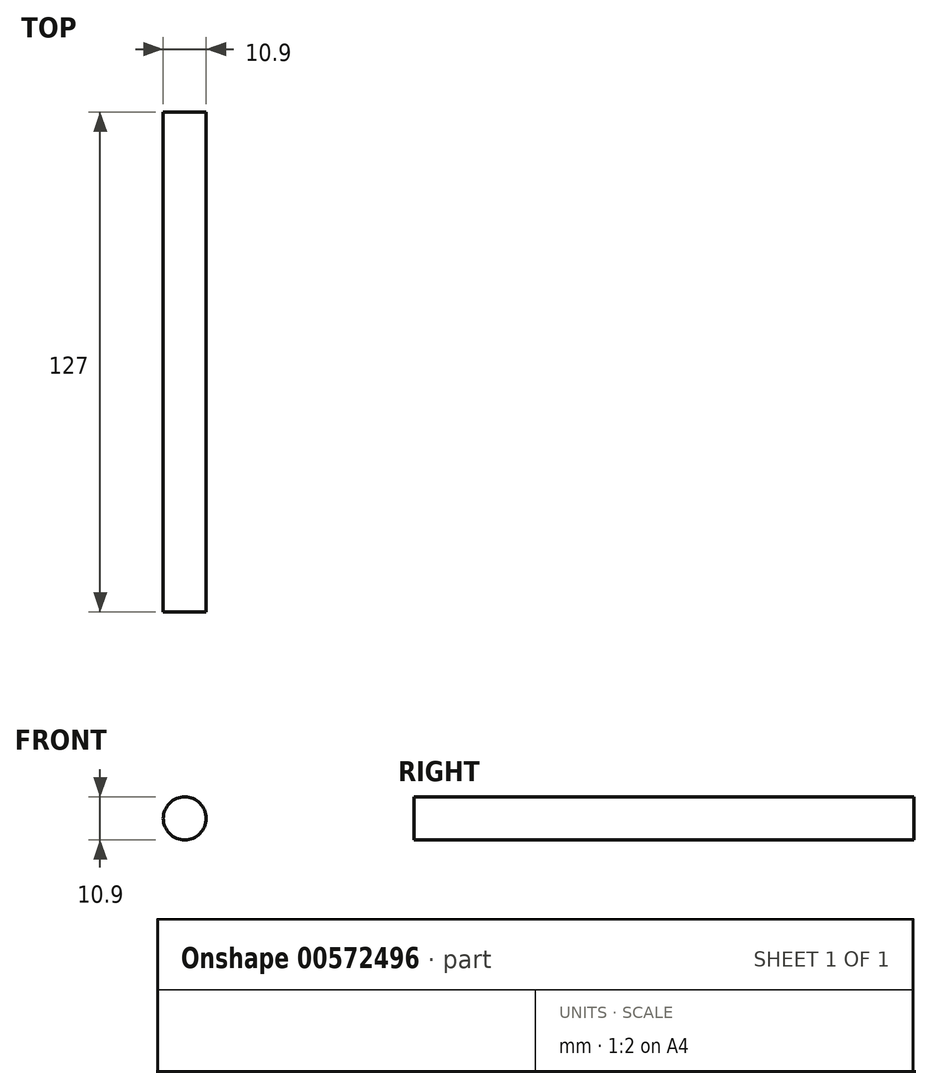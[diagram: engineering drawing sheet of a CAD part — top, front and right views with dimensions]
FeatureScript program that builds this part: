
annotation { "Feature Type Name" : "Feature", "Feature Type Description" : "" }
export const myFeature = defineFeature(function(context is Context, id is Id, definition is map)
    precondition{}
    {
        {
            var Q0;
            Q0=qCreatedBy(makeId("Front.planeOp"),FACE);
            var sketch = newSketch(context, id + "F0", { "sketchPlane" : qUnion([Q0])});
            skCircle(sketch, "E0", {"center": v(-4.03, 13.53) * mm, "radius": 5.45 * mm});
            skSolve(sketch);
        }
        {
            var Q0;
            Q0=makeQuery(id+"F0.imprint","IMPRINT",FACE,{"disambiguationData":[TD([[makeQuery(id+"F0.imprint","IMPRINT",EDGE,{"derivedFrom":sQuery(id+"F0.wireOp",EDGE,"E0")}),1.0]])]});
            extrude(context, id + "F1", {"entities" : qUnion([Q0]), "depth" : 127 * mm, "offsetDistance" : 25.4 * mm});
        }
    });
